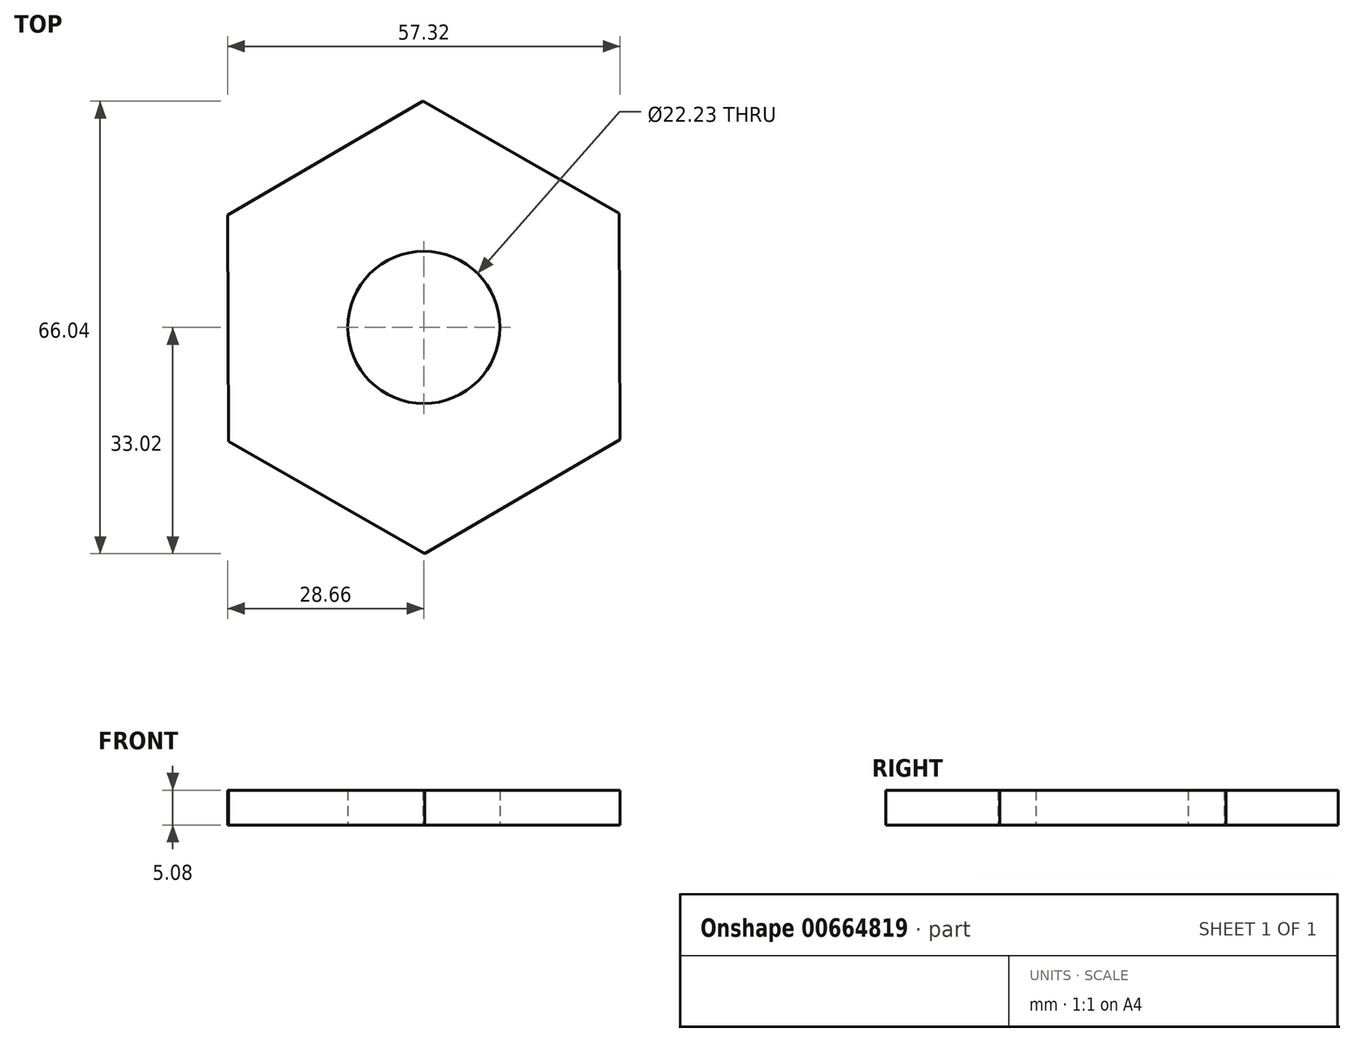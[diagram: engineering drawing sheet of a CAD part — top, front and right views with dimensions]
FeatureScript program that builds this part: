
annotation { "Feature Type Name" : "Feature", "Feature Type Description" : "" }
export const myFeature = defineFeature(function(context is Context, id is Id, definition is map)
    precondition{}
    {
        {
            var Q0;
            Q0=qCreatedBy(makeId("Top.planeOp"),FACE);
            var sketch = newSketch(context, id + "F0", { "sketchPlane" : qUnion([Q0])});
            skCircle(sketch, "E0.cCircle", {"center": v(0, 0) * mm, "radius": 28.6 * mm, "construction": true});
            skLineSegment(sketch, "E0.0", {"start": v(-0.13, 33.02) * mm, "end": v(28.53, 16.63) * mm});
            skLineSegment(sketch, "E0.1", {"start": v(28.53, 16.63) * mm, "end": v(28.66, -16.4) * mm});
            skLineSegment(sketch, "E0.2", {"start": v(28.66, -16.4) * mm, "end": v(0.13, -33.02) * mm});
            skLineSegment(sketch, "E0.3", {"start": v(0.13, -33.02) * mm, "end": v(-28.53, -16.63) * mm});
            skLineSegment(sketch, "E0.4", {"start": v(-28.53, -16.63) * mm, "end": v(-28.66, 16.4) * mm});
            skLineSegment(sketch, "E0.5", {"start": v(-28.66, 16.4) * mm, "end": v(-0.13, 33.02) * mm});
            skPoint(sketch, "E0.0.midPoint", {"position": v(14.2, 24.82) * mm});
            skCircle(sketch, "E1", {"center": v(0, 0) * mm, "radius": 11.11 * mm});
            skSolve(sketch);
        }
        {
            var Q0;
            Q0=makeQuery(id+"F0.imprint","IMPRINT",FACE,{"disambiguationData":[TD([[makeQuery(id+"F0.imprint","IMPRINT",EDGE,{"derivedFrom":sQuery(id+"F0.wireOp",EDGE,"E0.0")}),-1.0]])]});
            extrude(context, id + "F1", {"entities" : qUnion([Q0]), "depth" : 5.08 * mm, "offsetDistance" : 25.4 * mm});
        }
    });
